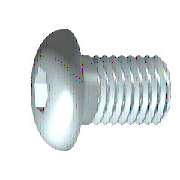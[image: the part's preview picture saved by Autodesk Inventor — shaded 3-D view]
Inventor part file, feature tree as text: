
AUTODESK INVENTOR PART (.ipt)
format: ipt  version: 2018 (Build 220112000, 112)  size: 204,800 bytes
history: native  units: mm (DEFAULTED — no unit token found)
features: sketch x2, extrude x1, plane x1, fillet x1
ambient origin geometry x7: Origin, YZ Plane, XY Plane, X Axis, Y Axis, Z Axis, Center Point
bodies: Solid1 (feature_tree), Body (feature_tree)
feature tree (5):
  extrude  "Slot"  Depth=2.2098mm
  plane  "Work Plane1"
  fillet  "Fillet2"  Radius=2.2098mm
  sketch  "Sketch1"  dims[d1=7.93476mm d2=1.59014mm d3=2.2098mm]
  sketch  "Sketch2"  dims[d4=1.3208mm d5=60.0deg d6=4.1656mm d7=4.1656mm d8=2.756963mm d9=7.9248mm d10=90.0deg d11=10.0mm d12=0.0mm d13=7.93476mm d14=0.0mm d15=0.486918mm d16=0.486918mm d17=1.9558mm d19=0.0mm d26=9.525mm d27=45.0deg d28=0.0mm d29=0.0mm d30=0.1mm]
